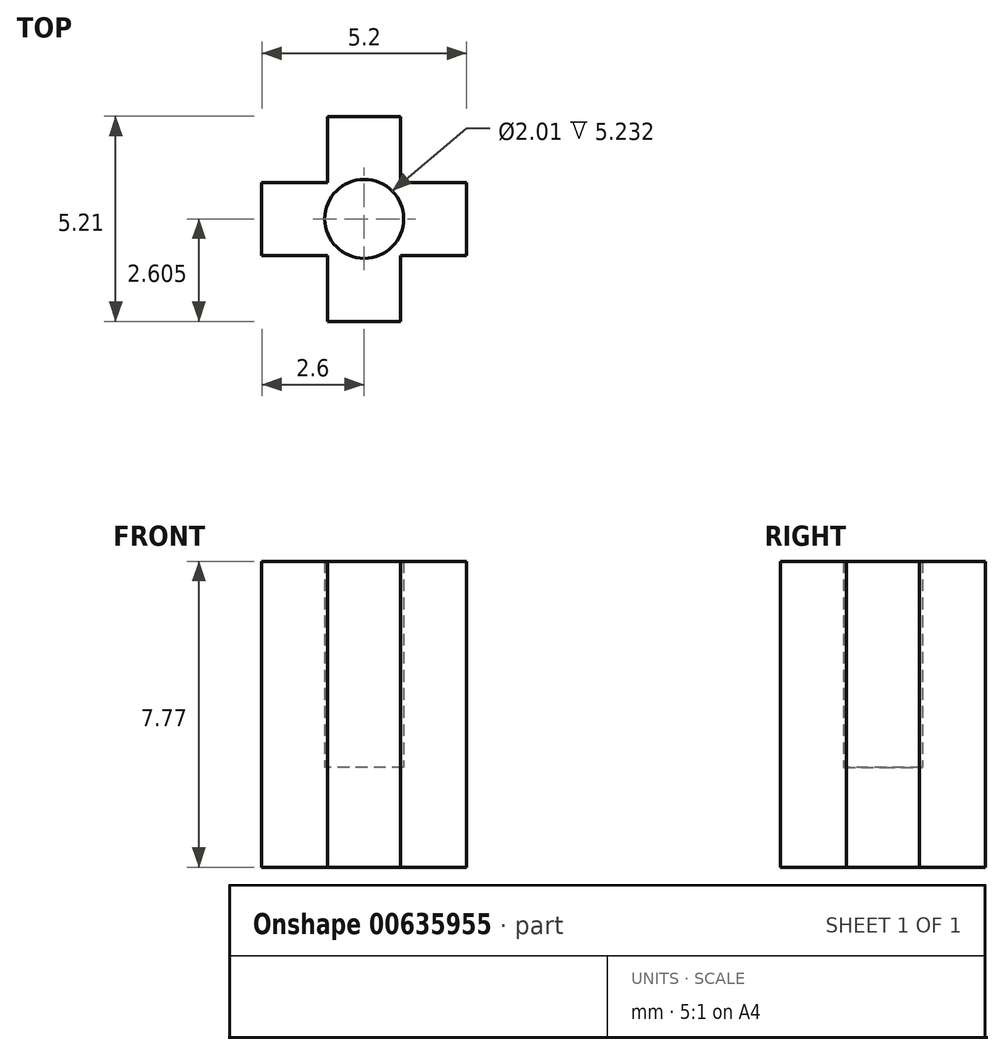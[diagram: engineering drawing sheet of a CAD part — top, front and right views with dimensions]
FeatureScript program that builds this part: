
annotation { "Feature Type Name" : "Feature", "Feature Type Description" : "" }
export const myFeature = defineFeature(function(context is Context, id is Id, definition is map)
    precondition{}
    {
        {
            var Q0;
            Q0=qCreatedBy(makeId("Top.planeOp"),FACE);
            var sketch = newSketch(context, id + "F0", { "sketchPlane" : qUnion([Q0])});
            skLineSegment(sketch, "E0.bottom", {"start": v(27.72, -6.68) * mm, "end": v(32.92, -6.68) * mm});
            skLineSegment(sketch, "E0.top", {"start": v(27.72, -8.53) * mm, "end": v(32.92, -8.53) * mm});
            skLineSegment(sketch, "E0.left", {"start": v(27.72, -6.68) * mm, "end": v(27.72, -8.53) * mm});
            skLineSegment(sketch, "E0.right", {"start": v(32.92, -6.68) * mm, "end": v(32.92, -8.53) * mm});
            skLineSegment(sketch, "E1.bottom", {"start": v(29.4, -5) * mm, "end": v(31.25, -5) * mm});
            skLineSegment(sketch, "E1.top", {"start": v(29.4, -10.2) * mm, "end": v(31.25, -10.2) * mm});
            skLineSegment(sketch, "E1.left", {"start": v(29.4, -5) * mm, "end": v(29.4, -10.2) * mm});
            skLineSegment(sketch, "E1.right", {"start": v(31.25, -5) * mm, "end": v(31.25, -10.2) * mm});
            skCircle(sketch, "E2", {"center": v(30.32, -7.6) * mm, "radius": 1 * mm});
            skPoint(sketch, "E2.centerSnap0", {"position": v(30.32, -8.53) * mm});
            skPoint(sketch, "E2.centerSnap1", {"position": v(29.4, -7.6) * mm});
            skSolve(sketch);
        }
        {
            var Q0;
            {var subQ1=sQuery(id+"F0.wireOp",EDGE,"E1.bottom");Q0=makeQuery(id+"F0.imprint","IMPRINT",FACE,{"disambiguationData":[TD([[makeQuery(id+"F0.imprint","IMPRINT",EDGE,{"derivedFrom":subQ1}),-1.0]])]});}
            var Q1;
            {var subQ0=sQuery(id+"F0.wireOp",EDGE,"E1.left");var subQ1=sQuery(id+"F0.wireOp",EDGE,"E0.bottom");var subQ2=makeQuery(id+"F0.imprint","INTERSECT",VERTEX,{"derivedFrom":[subQ1,subQ0]});Q1=makeQuery(id+"F0.imprint","IMPRINT",FACE,{"disambiguationData":[TD([[makeQuery(id+"F0.imprint","IMPRINT",EDGE,{"disambiguationData":[TD([[subQ2,-1.0]])],"derivedFrom":subQ1}),-1.0]])]});}
            var Q2;
            {var subQ5=sQuery(id+"F0.wireOp",EDGE,"E0.left");Q2=makeQuery(id+"F0.imprint","IMPRINT",FACE,{"disambiguationData":[TD([[makeQuery(id+"F0.imprint","IMPRINT",EDGE,{"derivedFrom":subQ5}),1.0]])]});}
            var Q3;
            {var subQ1=sQuery(id+"F0.wireOp",EDGE,"E1.top");Q3=makeQuery(id+"F0.imprint","IMPRINT",FACE,{"disambiguationData":[TD([[makeQuery(id+"F0.imprint","IMPRINT",EDGE,{"derivedFrom":subQ1}),1.0]])]});}
            var Q4;
            {var subQ5=sQuery(id+"F0.wireOp",EDGE,"E0.right");Q4=makeQuery(id+"F0.imprint","IMPRINT",FACE,{"disambiguationData":[TD([[makeQuery(id+"F0.imprint","IMPRINT",EDGE,{"derivedFrom":subQ5}),-1.0]])]});}
            var Q5;
            {var subQ0=sQuery(id+"F0.wireOp",EDGE,"E1.right");var subQ1=sQuery(id+"F0.wireOp",EDGE,"E0.bottom");var subQ2=makeQuery(id+"F0.imprint","INTERSECT",VERTEX,{"derivedFrom":[subQ1,subQ0]});Q5=makeQuery(id+"F0.imprint","IMPRINT",FACE,{"disambiguationData":[TD([[makeQuery(id+"F0.imprint","IMPRINT",EDGE,{"disambiguationData":[TD([[subQ2,1.0]])],"derivedFrom":subQ1}),-1.0]])]});}
            var Q6;
            {var subQ0=sQuery(id+"F0.wireOp",EDGE,"E1.right");var subQ1=sQuery(id+"F0.wireOp",EDGE,"E0.top");var subQ2=makeQuery(id+"F0.imprint","INTERSECT",VERTEX,{"derivedFrom":[subQ1,subQ0]});Q6=makeQuery(id+"F0.imprint","IMPRINT",FACE,{"disambiguationData":[TD([[makeQuery(id+"F0.imprint","IMPRINT",EDGE,{"disambiguationData":[TD([[subQ2,1.0]])],"derivedFrom":subQ1}),1.0]])]});}
            var Q7;
            {var subQ0=sQuery(id+"F0.wireOp",EDGE,"E1.left");var subQ1=sQuery(id+"F0.wireOp",EDGE,"E0.top");var subQ2=makeQuery(id+"F0.imprint","INTERSECT",VERTEX,{"derivedFrom":[subQ1,subQ0]});Q7=makeQuery(id+"F0.imprint","IMPRINT",FACE,{"disambiguationData":[TD([[makeQuery(id+"F0.imprint","IMPRINT",EDGE,{"disambiguationData":[TD([[subQ2,-1.0]])],"derivedFrom":subQ1}),1.0]])]});}
            extrude(context, id + "F1", {"entities" : qUnion([Q0, Q1, Q2, Q3, Q4, Q5, Q6, Q7]), "depth" : 7.77 * mm, "offsetDistance" : 25.4 * mm});
        }
        {
            var Q0;
            {var subQ0=sQuery(id+"F0.wireOp",EDGE,"E2");var subQ10=sQuery(id+"F0.wireOp",EDGE,"E0.bottom");var subQ11=makeQuery(id+"F0.imprint","INTERSECT",VERTEX,{"disambiguationData":[OD(0.0)],"derivedFrom":[subQ10,subQ0]});Q0=makeQuery(id+"F0.imprint","IMPRINT",FACE,{"disambiguationData":[TD([[makeQuery(id+"F0.imprint","IMPRINT",EDGE,{"disambiguationData":[TD([[subQ11,-1.0]])],"derivedFrom":subQ10}),-1.0]])]});}
            var Q1;
            {var subQ0=sQuery(id+"F0.wireOp",EDGE,"E2");var subQ1=sQuery(id+"F0.wireOp",EDGE,"E1.left");var subQ2=makeQuery(id+"F0.imprint","INTERSECT",VERTEX,{"disambiguationData":[OD(0.0)],"derivedFrom":[subQ1,subQ0]});Q1=makeQuery(id+"F0.imprint","IMPRINT",FACE,{"disambiguationData":[TD([[makeQuery(id+"F0.imprint","IMPRINT",EDGE,{"disambiguationData":[TD([[subQ2,-1.0]])],"derivedFrom":subQ1}),-1.0]])]});}
            var Q2;
            {var subQ0=sQuery(id+"F0.wireOp",EDGE,"E2");var subQ1=sQuery(id+"F0.wireOp",EDGE,"E0.top");var subQ2=makeQuery(id+"F0.imprint","INTERSECT",VERTEX,{"disambiguationData":[OD(0.0)],"derivedFrom":[subQ1,subQ0]});Q2=makeQuery(id+"F0.imprint","IMPRINT",FACE,{"disambiguationData":[TD([[makeQuery(id+"F0.imprint","IMPRINT",EDGE,{"disambiguationData":[TD([[subQ2,-1.0]])],"derivedFrom":subQ1}),-1.0]])]});}
            var Q3;
            {var subQ0=sQuery(id+"F0.wireOp",EDGE,"E2");var subQ1=sQuery(id+"F0.wireOp",EDGE,"E1.right");var subQ2=makeQuery(id+"F0.imprint","INTERSECT",VERTEX,{"disambiguationData":[OD(0.0)],"derivedFrom":[subQ1,subQ0]});Q3=makeQuery(id+"F0.imprint","IMPRINT",FACE,{"disambiguationData":[TD([[makeQuery(id+"F0.imprint","IMPRINT",EDGE,{"disambiguationData":[TD([[subQ2,-1.0]])],"derivedFrom":subQ1}),1.0]])]});}
            var Q4;
            {var subQ0=sQuery(id+"F0.wireOp",EDGE,"E2");var subQ1=sQuery(id+"F0.wireOp",EDGE,"E0.bottom");var subQ2=makeQuery(id+"F0.imprint","INTERSECT",VERTEX,{"disambiguationData":[OD(0.0)],"derivedFrom":[subQ1,subQ0]});Q4=makeQuery(id+"F0.imprint","IMPRINT",FACE,{"disambiguationData":[TD([[makeQuery(id+"F0.imprint","IMPRINT",EDGE,{"disambiguationData":[TD([[subQ2,-1.0]])],"derivedFrom":subQ1}),1.0]])]});}
            extrude(context, id + "F2", {"entities" : qUnion([Q0, Q1, Q2, Q3, Q4]), "operationType" : NewBodyOperationType.ADD, "depth" : 2.54 * mm, "offsetDistance" : 25.4 * mm});
        }
    });
